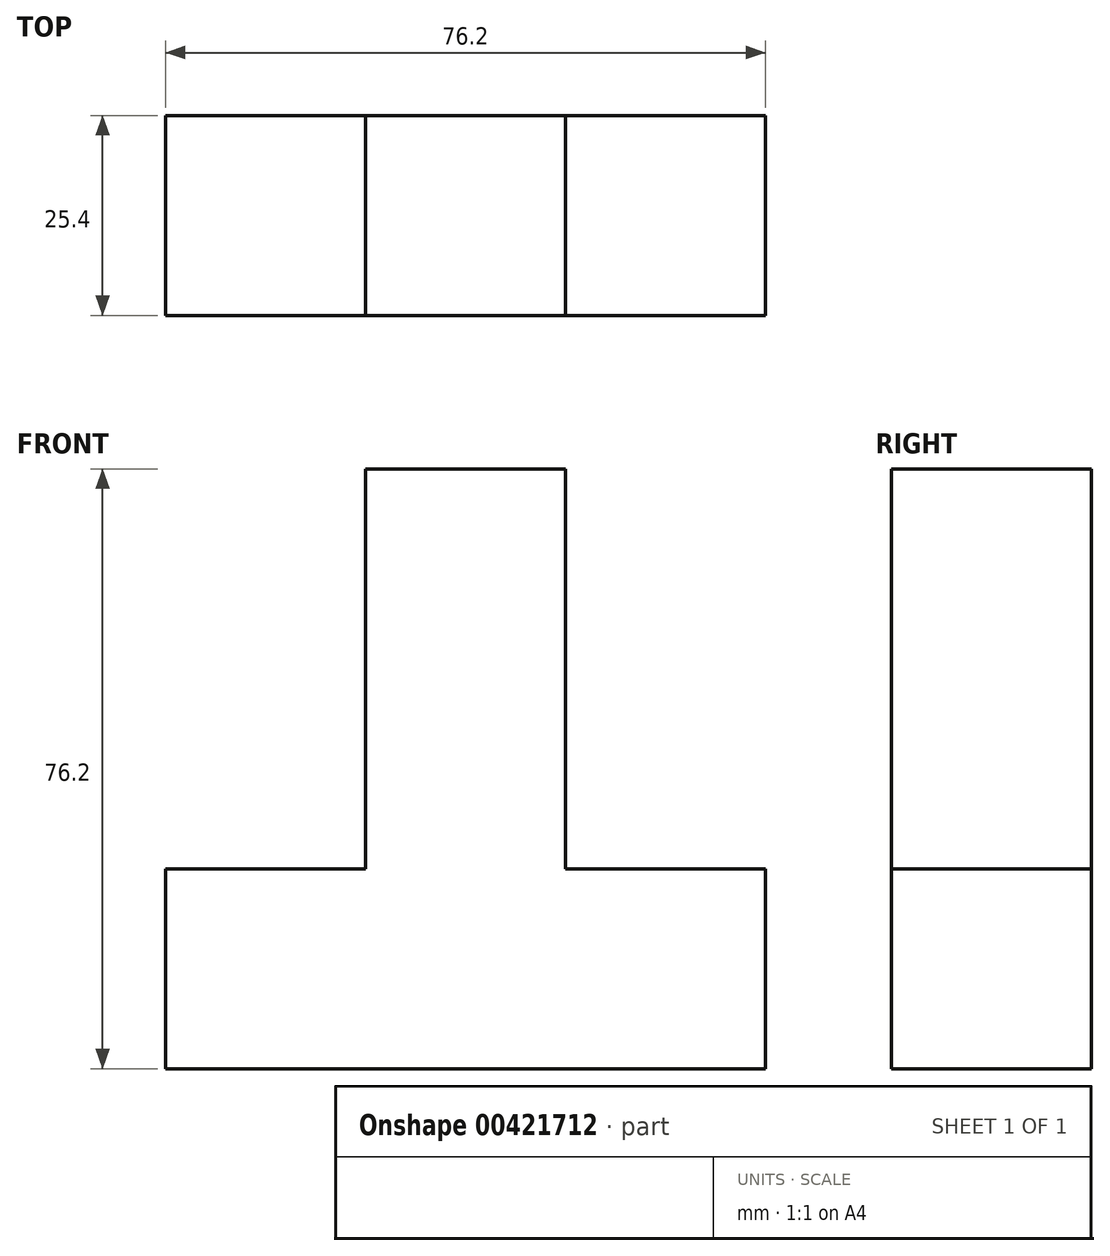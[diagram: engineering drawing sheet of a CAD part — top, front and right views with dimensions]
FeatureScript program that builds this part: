
annotation { "Feature Type Name" : "Feature", "Feature Type Description" : "" }
export const myFeature = defineFeature(function(context is Context, id is Id, definition is map)
    precondition{}
    {
        {
            var Q0;
            Q0=qCreatedBy(makeId("Front.planeOp"),FACE);
            var sketch = newSketch(context, id + "F0", { "sketchPlane" : qUnion([Q0])});
            skLineSegment(sketch, "E0", {"start": v(-55.44, 0) * mm, "end": v(-55.44, 25.4) * mm});
            skLineSegment(sketch, "E1", {"start": v(-55.44, 25.4) * mm, "end": v(-30.04, 25.4) * mm});
            skLineSegment(sketch, "E2", {"start": v(-30.04, 25.4) * mm, "end": v(-30.04, 76.2) * mm});
            skLineSegment(sketch, "E3", {"start": v(-30.04, 76.2) * mm, "end": v(-4.64, 76.2) * mm});
            skLineSegment(sketch, "E4", {"start": v(-4.64, 76.2) * mm, "end": v(-4.64, 25.4) * mm});
            skLineSegment(sketch, "E5", {"start": v(-4.64, 25.4) * mm, "end": v(20.76, 25.4) * mm});
            skLineSegment(sketch, "E6", {"start": v(20.76, 25.4) * mm, "end": v(20.76, 0) * mm});
            skLineSegment(sketch, "E7", {"start": v(20.76, 0) * mm, "end": v(-55.44, 0) * mm});
            skSolve(sketch);
        }
        {
            var Q0;
            Q0=makeQuery(id+"F0.imprint","IMPRINT",FACE,{"disambiguationData":[TD([[makeQuery(id+"F0.imprint","IMPRINT",EDGE,{"derivedFrom":sQuery(id+"F0.wireOp",EDGE,"E0")}),-1.0]])]});
            extrude(context, id + "F1", {"entities" : qUnion([Q0]), "depth" : 25.4 * mm});
        }
    });
